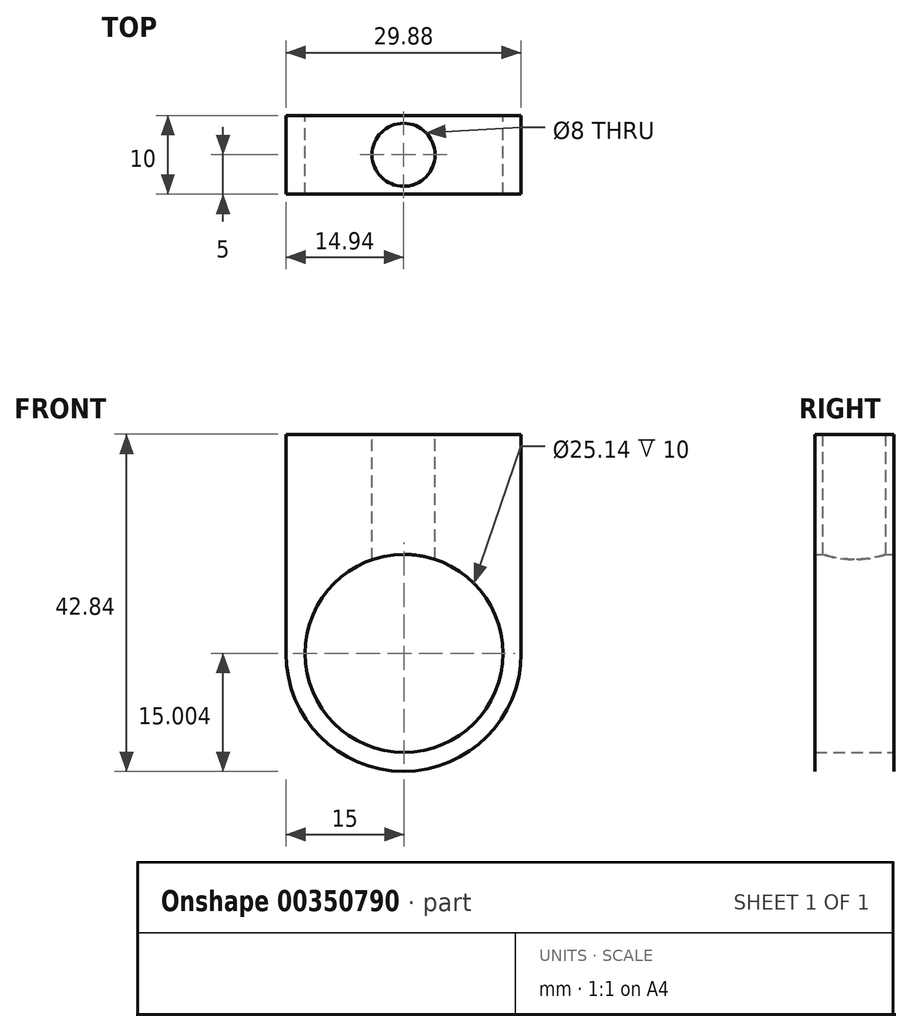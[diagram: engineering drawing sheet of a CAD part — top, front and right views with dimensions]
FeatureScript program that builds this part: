
annotation { "Feature Type Name" : "Feature", "Feature Type Description" : "" }
export const myFeature = defineFeature(function(context is Context, id is Id, definition is map)
    precondition{}
    {
        {
            var Q0;
            Q0=qCreatedBy(makeId("Front.planeOp"),FACE);
            var sketch = newSketch(context, id + "F0", { "sketchPlane" : qUnion([Q0])});
            skLineSegment(sketch, "E0.bottom", {"start": v(9.3, 9.2) * mm, "end": v(-20.58, 9.2) * mm});
            skLineSegment(sketch, "E0.top", {"start": v(-5.58, -33.64) * mm, "end": v(-5.7, -33.64) * mm});
            skLineSegment(sketch, "E0.left", {"start": v(9.3, 9.2) * mm, "end": v(9.3, -18.64) * mm});
            skLineSegment(sketch, "E0.right", {"start": v(-20.58, 9.2) * mm, "end": v(-20.58, -18.64) * mm});
            skPoint(sketch, "E1.visualSharp", {"position": v(9.3, -33.64) * mm});
            skArc(sketch, "E1.filletArc", {"start": v(-5.7, -33.64) * mm, "mid": v(4.9, -29.24) * mm, "end": v(9.3, -18.64) * mm});
            skPoint(sketch, "E2.visualSharp", {"position": v(-20.58, -33.64) * mm});
            skArc(sketch, "E2.filletArc", {"start": v(-20.58, -18.64) * mm, "mid": v(-16.19, -29.24) * mm, "end": v(-5.58, -33.64) * mm});
            skCircle(sketch, "E3", {"center": v(-5.58, -18.64) * mm, "radius": 12.57 * mm});
            skSolve(sketch);
        }
        {
            var Q0;
            Q0=makeQuery(id+"F0.imprint","IMPRINT",FACE,{"disambiguationData":[TD([[makeQuery(id+"F0.imprint","IMPRINT",EDGE,{"derivedFrom":sQuery(id+"F0.wireOp",EDGE,"E0.bottom")}),1.0]])]});
            extrude(context, id + "F1", {"entities" : qUnion([Q0]), "depth" : 10 * mm});
        }
        {
            var Q0;
            Q0=makeQuery(id+"F1.opExtrude","SWEPT_FACE",FACE,{"disambiguationData":[OSD([sQuery(id+"F0.wireOp",EDGE,"E0.bottom")])]});
            var sketch = newSketch(context, id + "F2", { "sketchPlane" : qUnion([Q0])});
            skLineSegment(sketch, "E4", {"start": v(-20.58, 0) * mm, "end": v(-5.64, 0) * mm});
            skCircle(sketch, "E5", {"center": v(-5.64, -5) * mm, "radius": 4 * mm});
            skSolve(sketch);
        }
        {
            var Q0;
            Q0 = qSketchRegion(id + "F2", true);
            extrude(context, id + "F3", {"entities" : qUnion([Q0]), "operationType" : NewBodyOperationType.REMOVE, "oppositeDirection" : true, "depth" : 25 * mm});
        }
    });
